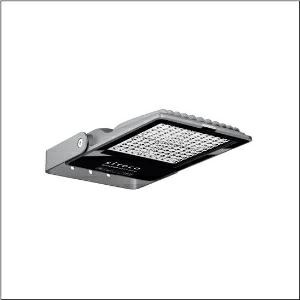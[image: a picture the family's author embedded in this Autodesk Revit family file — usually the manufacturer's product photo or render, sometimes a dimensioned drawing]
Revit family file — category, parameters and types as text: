
# Revit family: sicompact_r__31_mini___pl32_5xa7571b1k23_124a
name_source: partatom
category: Lighting Fixtures
units: mm (PartAtom-declared; Revit-internal decimal feet)

## family parameters
Cut with Voids When Loaded = No
Host = Face
Light Source = No
Part Type = Normal
Room Calculation Point = No
Round Connector Dimension = Use Diameter
Shared = No

## types (1)
- SiCompact® 31 mini  PL32 (1 x LED, 8000 lm, 48 W, 3000K)
    Apparent Load = 48 VA
    CIE Flux Codes = 32 69 98 100 100
    Color Rendering = 70
    Color Temperature = 3000K
    Default Elevation = 1800 mm
    Description = SiCompact® 31 mini, floodlight, primary light control with lens, of plastic, of toughened safety glass, transparent, light distribution: PL32, light emission: direct distribution, primary light characteristic: asymmetric, installation type: surface-mounted, LED, High Power LED, rated luminous flux: 8.000lm, luminous efficacy: 167lm/W, light colour: 730, colour temperature: 3000K, control gear: ECG, with cable, 3x 1.5mm², mains connection: 220..240V, AC, 50/60Hz, connection cable pre-assembled, cable length: 2m, rated input power: 48W, of diecast aluminium, specular, metallic grey (RAL 9006), length: 461mm, width: 261mm, height: 62mm, bracket, of sheet steel, coated, metallic grey (RAL 9006), ON/OFF, protection rating (complete): IP66, insulation class (complete): insulation class I (protective earthing), certification: CE, ENEC, impact resistance: IK08, permissible operating ambient temperature: -40..+45°C, packaging unit: 1 piece

Light Distribution: PL32
    Height = 62 mm  [stored 0.203412 ft]
    Lamp = 1 x LED
    Lamp Light Flux = 8000 lm
    Lamp Power = 48 W
    Lamp count = 1
    Length = 460 mm
    Luminous efficacy = 167 lm/W
    Manufacturer = Siteco
    ModVariant = No
    Model = 5XA7571B1K23
    Mounting Place = Wall
    Mounting Type = Surface mounted
    Number of Poles = 1
    OnlyDefault = Yes
    Power Factor = 1
    Product Name = SiCompact® 31 mini | PL32
    Product group = floodlight | wall mounted
    ProductGroupID = 2001
    Protection Class = Protection class I
    Protection Degree = IP 66
    RLX_Detail_Level = 1
    RLX_Emergency_Light_Flux = 0 lm
    RLX_Emergency_Type = 0
    RLX_Emergency_Type_DB = No
    RlxData = <blob elided: 126597 chars, md5=de123127>
    Socket = socket
    Standby Power = 0 W
    System Light Flux = 8000 lm
    System Power = 48 W
    Type Comments = Product without accessories
    Type Image = l_1006951.jpg
    URL = http://relux.com
    VarID = ---
    Voltage = 0 V
    Weight = 0.00 kg
    Width = 260 mm

note: [stored X ft] marks values corroborated as IEEE doubles in the binary element streams (Revit-internal decimal feet)

## geometry (parser evidence)
native form markers: Blend x4, Sweep x12
no freeform markers — native parametric forms only
